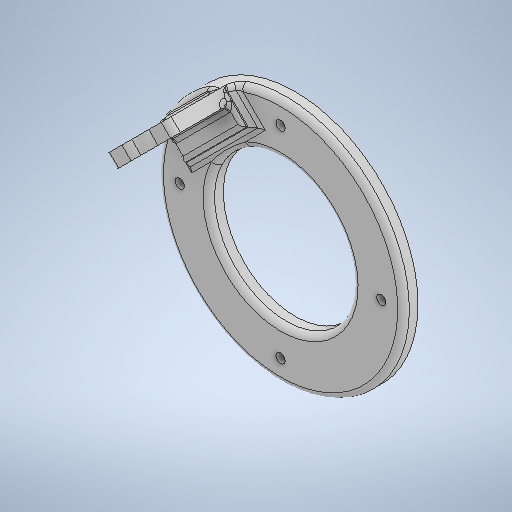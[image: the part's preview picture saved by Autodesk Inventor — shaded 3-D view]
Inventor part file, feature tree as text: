
AUTODESK INVENTOR PART (.ipt)
format: ipt  version: 2025.1 (Build 291241000, 241)  size: 712,704 bytes
history: native  units: mm
features: fillet x11, extrude x6, sketch x5, chamfer x3
ambient origin geometry x8: Origin, YZ Plane, XZ Plane, XY Plane, X Axis, Y Axis, Z Axis, Center Point
bodies: Solid1 (feature_tree)
feature tree (25):
  extrude  "Extrusion1"  Depth=5.0mm TaperAngle=0.0deg
  extrude  "Extrusion2"  Depth=5.0mm TaperAngle=0.0deg
  sketch  "Sketch4"  dims[d7=3.2mm d8=3.2mm]
  extrude  "Extrusion3"  Depth=3.2mm
  extrude  "Extrusion4"  Depth=34.85mm
  extrude  "Extrusion5"  Depth=3.2mm
  extrude  "Extrusion6"  Depth=69.7mm
  fillet  "Fillet1"  Radius=69.7mm
  fillet  "Fillet2"  Radius=34.85mm
  chamfer  "Chamfer1"  Distance=34.85mm
  chamfer  "Chamfer2"  Distance=5.0mm
  chamfer  "Chamfer3"  Distance=49.285343mm
  fillet  "Fillet3"  Radius=49.285343mm
  fillet  "Fillet4"  Radius=10.0mm
  fillet  "Fillet5"  Radius=10.0mm
  fillet  "Fillet6"  Radius=29.312869mm
  fillet  "Fillet7"  Radius=13.70143mm
  fillet  "Fillet8"  Radius=3.0mm
  fillet  "Fillet9"  Radius=19.0mm
  fillet  "Fillet10"  Radius=4.5mm
  fillet  "Fillet11"  Radius=29.311768mm
  sketch  "Sketch1"  dims[d0=85.0mm d1=5.0mm d2=0.0mm]
  sketch  "Sketch2"  dims[d3=49.6mm d4=5.0mm d5=0.0mm]
  sketch  "Sketch5"  dims[d11=34.85mm d13=34.85mm]
  sketch  "Sketch6"  dims[d16=3.2mm d17=3.2mm d19=69.7mm d20=69.7mm d21=34.85mm d22=34.85mm d23=5.0mm d24=0.0mm d25=49.285343mm d26=49.285343mm d27=10.0mm d28=10.0mm d29=29.312869mm d30=13.70143mm d31=3.0mm d32=0.0mm d34=19.0mm d35=0.0mm d37=4.5mm d38=29.311768mm d39=4.5mm d40=29.311768mm d41=9.2mm d44=14.655884mm d45=14.6605mm d46=4.6mm d47=4.604616mm d48=14.0mm d49=19.0mm d50=0.0mm d51=2.0mm d52=2.0mm d53=2.5mm d54=2.0mm d55=45.0deg d56=1.0mm d57=2.0mm d58=45.0deg d59=1.0mm d60=2.0mm d61=45.0deg d62=2.0mm d63=2.0mm d64=2.0mm d65=2.0mm d66=2.0mm d67=2.0mm d68=2.0mm d69=2.0mm d70=2.0mm]
